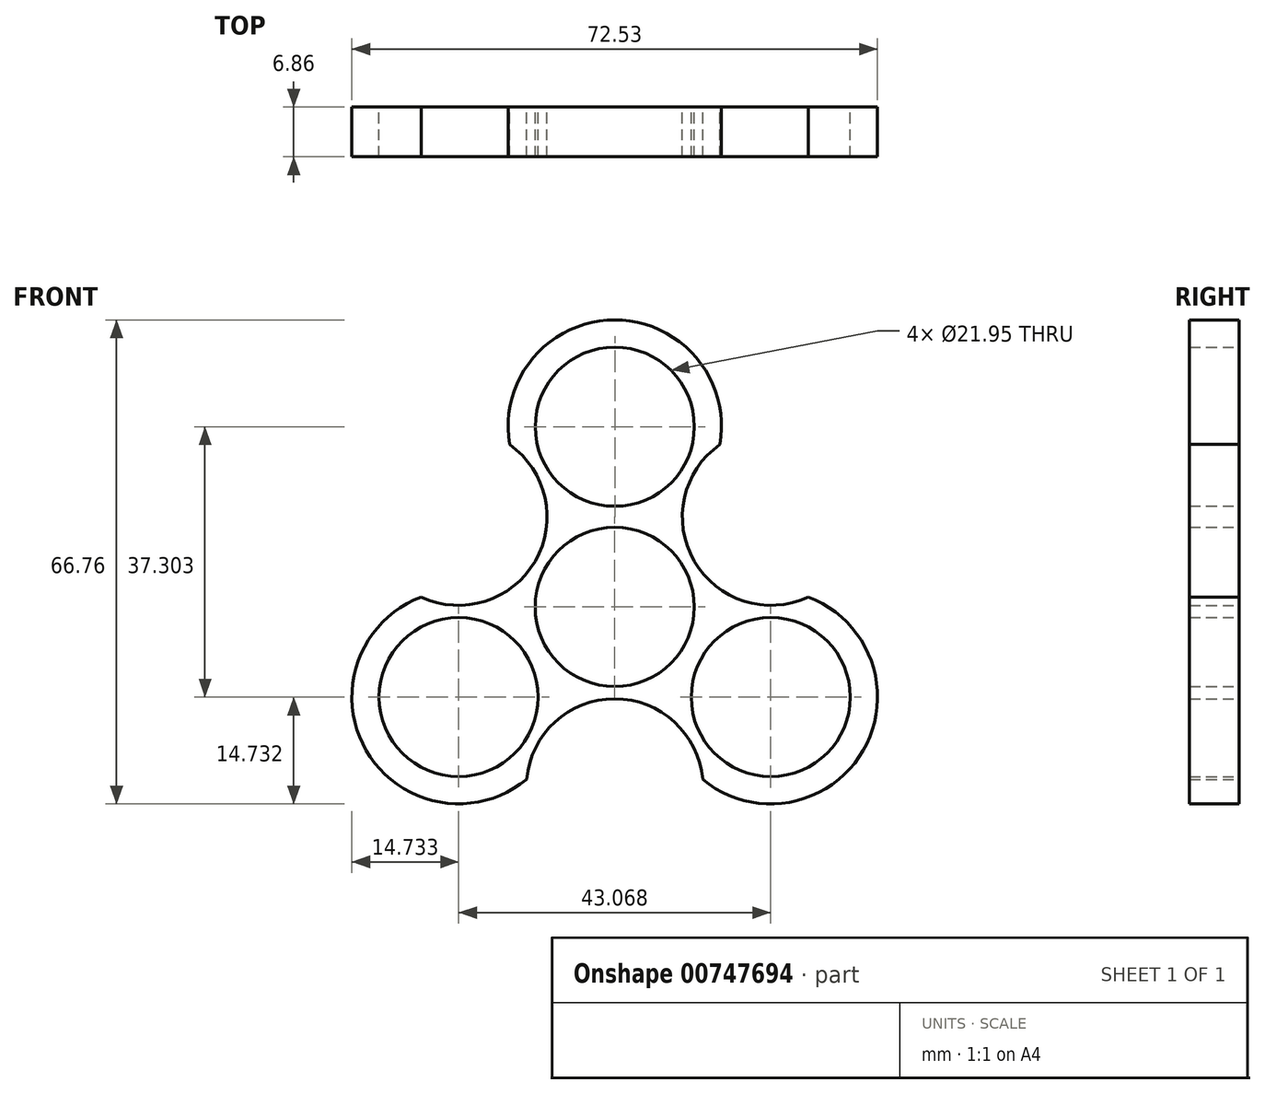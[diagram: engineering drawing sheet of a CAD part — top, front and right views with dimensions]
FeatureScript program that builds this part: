
annotation { "Feature Type Name" : "Feature", "Feature Type Description" : "" }
export const myFeature = defineFeature(function(context is Context, id is Id, definition is map)
    precondition{}
    {
        {
            var Q0;
            Q0=qCreatedBy(makeId("Front.planeOp"),FACE);
            var sketch = newSketch(context, id + "F0", { "sketchPlane" : qUnion([Q0])});
            skCircle(sketch, "E0.cCircle", {"center": v(0, 0) * mm, "radius": 21.53 * mm, "construction": true});
            skLineSegment(sketch, "E0.0", {"start": v(0, 24.87) * mm, "end": v(21.54, 12.43) * mm, "construction": true});
            skLineSegment(sketch, "E0.1", {"start": v(21.54, 12.43) * mm, "end": v(21.53, -12.44) * mm, "construction": true});
            skLineSegment(sketch, "E0.2", {"start": v(21.53, -12.44) * mm, "end": v(0, -24.87) * mm, "construction": true});
            skLineSegment(sketch, "E0.3", {"start": v(0, -24.87) * mm, "end": v(-21.54, -12.43) * mm, "construction": true});
            skLineSegment(sketch, "E0.4", {"start": v(-21.54, -12.43) * mm, "end": v(-21.53, 12.44) * mm, "construction": true});
            skLineSegment(sketch, "E0.5", {"start": v(-21.53, 12.44) * mm, "end": v(0, 24.87) * mm, "construction": true});
            skPoint(sketch, "E0.0.midPoint", {"position": v(10.77, 18.65) * mm});
            skCircle(sketch, "E1", {"center": v(0, 0) * mm, "radius": 10.97 * mm});
            skCircle(sketch, "E2", {"center": v(0, 24.87) * mm, "radius": 10.97 * mm});
            skLineSegment(sketch, "E3", {"start": v(-6.83, 13.76) * mm, "end": v(-6.83, 13.76) * mm});
            skLineSegment(sketch, "E4", {"start": v(-15.36, 0.2) * mm, "end": v(-15.36, 0.2) * mm});
            skLineSegment(sketch, "E5", {"start": v(-7.79, -13.25) * mm, "end": v(-7.79, -13.25) * mm});
            skPoint(sketch, "E6.3.internal.snap0", {"position": v(-21.53, 0) * mm});
            skCircle(sketch, "E7.MirrorC", {"center": v(-21.54, 12.43) * mm, "radius": 12.2 * mm});
            skCircle(sketch, "E8", {"center": v(0, -24.87) * mm, "radius": 12.2 * mm});
            skCircle(sketch, "E9", {"center": v(-21.54, -12.43) * mm, "radius": 10.97 * mm});
            skCircle(sketch, "E10", {"center": v(21.53, -12.44) * mm, "radius": 10.97 * mm});
            skArc(sketch, "E11", {"start": v(14.53, 22.42) * mm, "mid": v(0, 39.6) * mm, "end": v(-14.52, 22.4) * mm});
            skArc(sketch, "E12", {"start": v(9.38, 13.5) * mm, "mid": v(32.1, 6.32) * mm, "end": v(14.53, 22.42) * mm});
            skArc(sketch, "E13", {"start": v(14.53, 22.42) * mm, "mid": v(10.97, 18.53) * mm, "end": v(9.38, 13.5) * mm});
            skArc(sketch, "E14", {"start": v(12.14, -23.78) * mm, "mid": v(34.28, -19.81) * mm, "end": v(26.68, 1.36) * mm});
            skArc(sketch, "E15", {"start": v(-26.7, 1.37) * mm, "mid": v(-34.29, -19.8) * mm, "end": v(-12.15, -23.78) * mm});
            skSolve(sketch);
        }
        {
            var Q0;
            Q0=makeQuery(id+"F0.imprint","IMPRINT",FACE,{"disambiguationData":[TD([[makeQuery(id+"F0.imprint","IMPRINT",EDGE,{"derivedFrom":sQuery(id+"F0.wireOp",EDGE,"E1")}),-1.0]])]});
            extrude(context, id + "F1", {"entities" : qUnion([Q0]), "depth" : 6.86 * mm, "offsetDistance" : 25.4 * mm});
        }
    });
